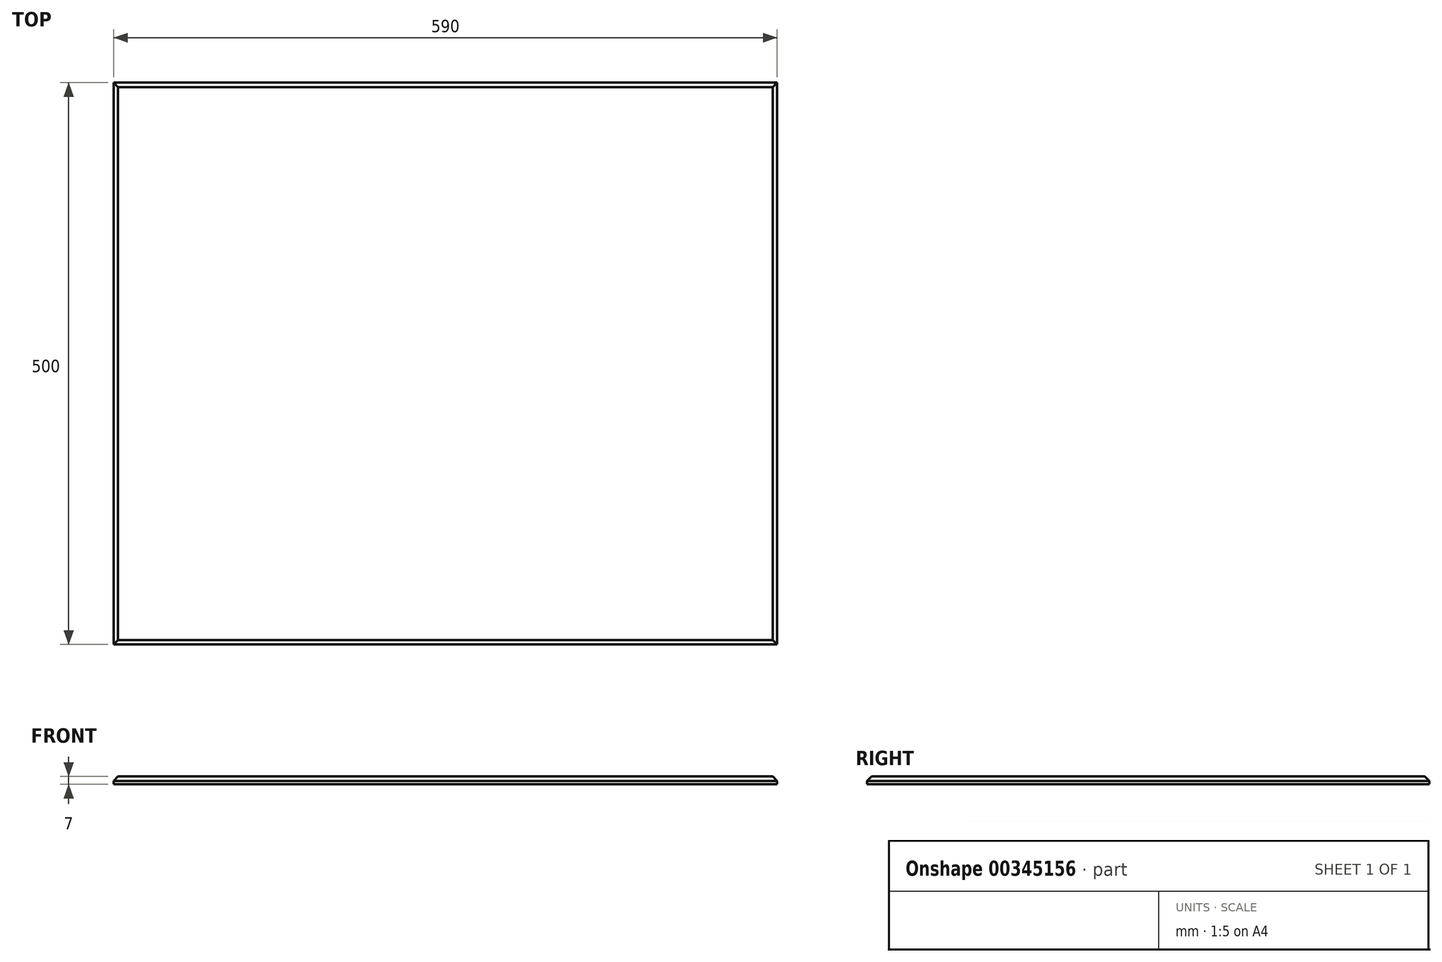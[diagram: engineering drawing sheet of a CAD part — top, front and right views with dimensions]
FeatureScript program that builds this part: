
annotation { "Feature Type Name" : "Feature", "Feature Type Description" : "" }
export const myFeature = defineFeature(function(context is Context, id is Id, definition is map)
    precondition{}
    {
        {
            var Q0;
            Q0=qCreatedBy(makeId("Top.planeOp"),FACE);
            var sketch = newSketch(context, id + "F0", { "sketchPlane" : qUnion([Q0])});
            skLineSegment(sketch, "E0.bottom", {"start": v(0, 0) * mm, "end": v(44.84, 0) * mm});
            skLineSegment(sketch, "E0.top", {"start": v(0, 43.04) * mm, "end": v(44.84, 43.04) * mm});
            skLineSegment(sketch, "E0.left", {"start": v(0, 0) * mm, "end": v(0, 43.04) * mm});
            skLineSegment(sketch, "E0.right", {"start": v(44.84, 0) * mm, "end": v(44.84, 43.04) * mm});
            skSolve(sketch);
        }
        {
            var Q0;
            Q0=makeQuery(id+"F0.imprint","IMPRINT",FACE,{"disambiguationData":[TD([[makeQuery(id+"F0.imprint","IMPRINT",EDGE,{"derivedFrom":sQuery(id+"F0.wireOp",EDGE,"E0.bottom")}),1.0]])]});
            extrude(context, id + "F1", {"entities" : qUnion([Q0]), "depth" : 7 * mm});
        }
        {
            var Q0;
            Q0=makeQuery(id+"F1.opExtrude","SWEPT_FACE",FACE,{"disambiguationData":[OSD([sQuery(id+"F0.wireOp",EDGE,"E0.left")])]});
            extrude(context, id + "F2", {"entities" : qUnion([Q0]), "operationType" : NewBodyOperationType.ADD, "oppositeDirection" : true, "depth" : 590 * mm});
        }
        {
            var Q0;
            {var subQ0=sQuery(id+"F0.wireOp",EDGE,"E0.bottom");Q0=makeQuery(id+"F2.boolean.opBoolean","MERGE",FACE,{"derivedFrom":[makeQuery(id+"F1.opExtrude","SWEPT_FACE",FACE,{"disambiguationData":[OSD([subQ0])]}),makeQuery(id+"F2.opExtrude","SWEPT_FACE",FACE,{"disambiguationData":[OSD([subQ0,sQuery(id+"F0.wireOp",EDGE,"E0.left")])]})]});}
            extrude(context, id + "F3", {"entities" : qUnion([Q0]), "operationType" : NewBodyOperationType.ADD, "oppositeDirection" : true, "depth" : 500 * mm});
        }
        {
            var Q0;
            {var subQ0=sQuery(id+"F0.wireOp",EDGE,"E0.left");var subQ1=sQuery(id+"F0.wireOp",EDGE,"E0.bottom");Q0=makeQuery(id+"F3.boolean.opBoolean","MERGE",FACE,{"derivedFrom":[makeQuery(id+"F2.boolean.opBoolean","MERGE",FACE,{"derivedFrom":[makeQuery(id+"F1.opExtrude","CAP_FACE",FACE,{"disambiguationData":[OSD([subQ1,sQuery(id+"F0.wireOp",EDGE,"E0.top"),subQ0,sQuery(id+"F0.wireOp",EDGE,"E0.right")])],"isStart":false}),makeQuery(id+"F2.opExtrude","SWEPT_FACE",FACE,{"disambiguationData":[OSD([subQ0]),TDD([makeQuery(id+"F1.opExtrude","CAP_EDGE",EDGE,{"disambiguationData":[OSD([subQ0])],"isStart":false})])]})]}),makeQuery(id+"F3.opExtrude","SWEPT_FACE",FACE,{"disambiguationData":[OSD([subQ1,subQ0]),TDD([makeQuery(id+"F2.boolean.opBoolean","MERGE",EDGE,{"derivedFrom":[makeQuery(id+"F1.opExtrude","CAP_EDGE",EDGE,{"disambiguationData":[OSD([subQ1])],"isStart":false}),makeQuery(id+"F2.opExtrude","SWEPT_EDGE",EDGE,{"disambiguationData":[OSD([subQ1,subQ0]),TDD([makeQuery(id+"F1.opExtrude","CAP_VERTEX",VERTEX,{"disambiguationData":[OSD([subQ1,subQ0])],"isStart":false})])]})]})])]})]});}
            chamfer(context, id + "F4", {"entities" : qUnion([Q0]), "width" : 4 * mm, "tangentPropagation" : true});
        }
    });
